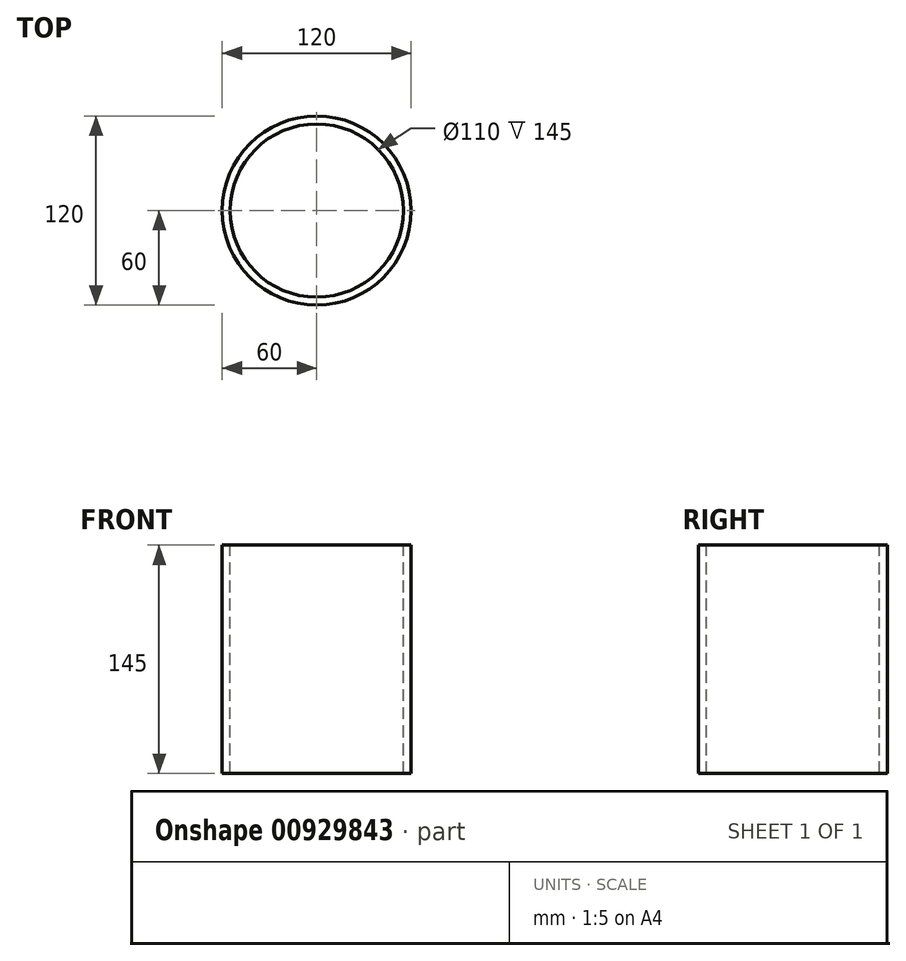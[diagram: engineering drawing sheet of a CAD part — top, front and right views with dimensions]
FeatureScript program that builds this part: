
annotation { "Feature Type Name" : "Feature", "Feature Type Description" : "" }
export const myFeature = defineFeature(function(context is Context, id is Id, definition is map)
    precondition{}
    {
        {
            var Q0;
            Q0=qCreatedBy(makeId("Top.planeOp"),FACE);
            var sketch = newSketch(context, id + "F0", { "sketchPlane" : qUnion([Q0])});
            skCircle(sketch, "E0", {"center": v(0, 0) * mm, "radius": 60 * mm});
            skSolve(sketch);
        }
        {
            var Q0;
            Q0=makeQuery(id+"F0.imprint","IMPRINT",FACE,{"disambiguationData":[TD([[makeQuery(id+"F0.imprint","IMPRINT",EDGE,{"derivedFrom":sQuery(id+"F0.wireOp",EDGE,"E0")}),1.0]])]});
            extrude(context, id + "F1", {"entities" : qUnion([Q0]), "depth" : 145 * mm, "offsetDistance" : 25 * mm});
        }
        {
            var Q0;
            Q0=makeQuery(id+"F1.opExtrude","CAP_FACE",FACE,{"disambiguationData":[OSD([sQuery(id+"F0.wireOp",EDGE,"E0")])],"isStart":false});
            var sketch = newSketch(context, id + "F2", { "sketchPlane" : qUnion([Q0])});
            skSolve(sketch);
        }
        {
            var Q0;
            Q0=makeQuery(id+"F2.imprint","IMPRINT",FACE,{"disambiguationData":[TD([[makeQuery(id+"F2.imprint","IMPRINT",EDGE,{"derivedFrom":makeQuery(id+"F1.opExtrude","CAP_EDGE",EDGE,{"disambiguationData":[OSD([sQuery(id+"F0.wireOp",EDGE,"E0")])],"isStart":false})}),1.0]])]});
            var sketch = newSketch(context, id + "F3", { "sketchPlane" : qUnion([Q0])});
            skCircle(sketch, "E1", {"center": v(0, 0) * mm, "radius": 55 * mm});
            skSolve(sketch);
        }
        {
            var Q0;
            Q0=makeQuery(id+"F3.imprint","IMPRINT",FACE,{"disambiguationData":[TD([[makeQuery(id+"F3.imprint","IMPRINT",EDGE,{"derivedFrom":sQuery(id+"F3.wireOp",EDGE,"E1")}),1.0]])]});
            extrude(context, id + "F4", {"entities" : qUnion([Q0]), "operationType" : NewBodyOperationType.REMOVE, "depth" : -230 * mm, "offsetDistance" : 25 * mm});
        }
    });
